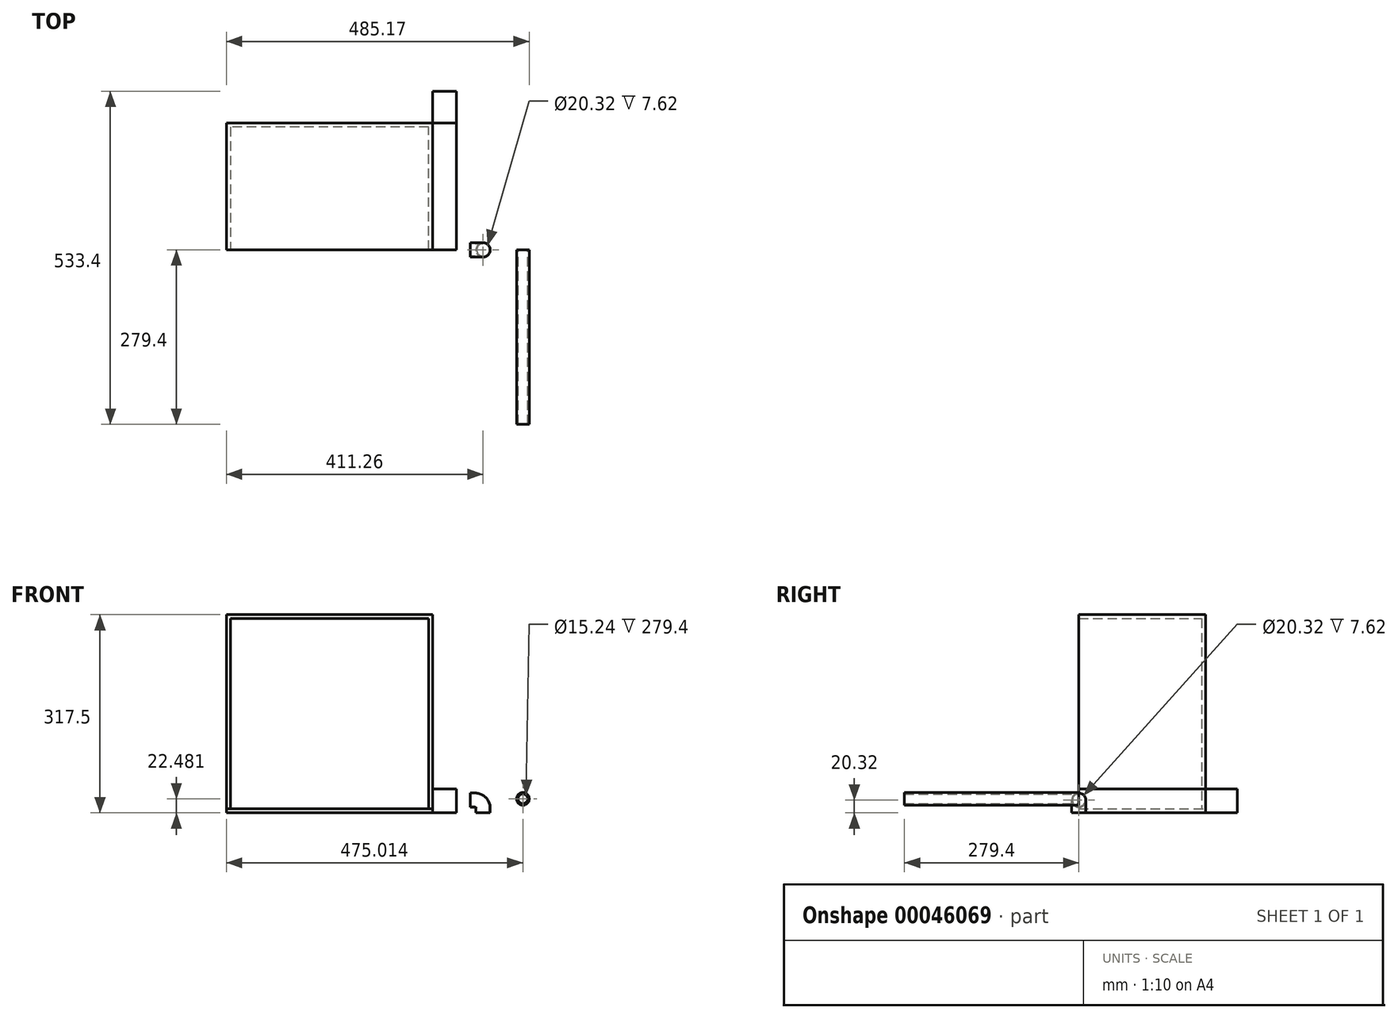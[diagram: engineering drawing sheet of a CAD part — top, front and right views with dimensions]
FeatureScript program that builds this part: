
annotation { "Feature Type Name" : "Feature", "Feature Type Description" : "" }
export const myFeature = defineFeature(function(context is Context, id is Id, definition is map)
    precondition{}
    {
        {
            var Q0;
            Q0=qCreatedBy(makeId("Front.planeOp"),FACE);
            var sketch = newSketch(context, id + "F0", { "sketchPlane" : qUnion([Q0])});
            skLineSegment(sketch, "E0.bottom", {"start": v(0, 0) * mm, "end": v(38.1, 0) * mm});
            skLineSegment(sketch, "E0.top", {"start": v(0, 38.5) * mm, "end": v(38.1, 38.5) * mm});
            skLineSegment(sketch, "E0.left", {"start": v(0, 0) * mm, "end": v(0, 38.5) * mm});
            skLineSegment(sketch, "E0.right", {"start": v(38.1, 0) * mm, "end": v(38.1, 38.5) * mm});
            skSolve(sketch);
        }
        {
            var Q0;
            Q0=makeQuery(id+"F0.imprint","IMPRINT",FACE,{"disambiguationData":[TD([[makeQuery(id+"F0.imprint","IMPRINT",EDGE,{"derivedFrom":sQuery(id+"F0.wireOp",EDGE,"E0.bottom")}),1.0]])]});
            extrude(context, id + "F1", {"entities" : qUnion([Q0]), "oppositeDirection" : true, "depth" : 254 * mm});
        }
        {
            var Q0;
            Q0=makeQuery(id+"F0.imprint","IMPRINT",FACE,{"disambiguationData":[TD([[makeQuery(id+"F0.imprint","IMPRINT",EDGE,{"derivedFrom":sQuery(id+"F0.wireOp",EDGE,"E0.bottom")}),1.0]])]});
            extrude(context, id + "F2", {"entities" : qUnion([Q0]), "oppositeDirection" : true, "depth" : 203.2 * mm});
        }
        {
            var Q0;
            Q0=qCreatedBy(makeId("Top.planeOp"),FACE);
            var sketch = newSketch(context, id + "F3", { "sketchPlane" : qUnion([Q0])});
            skLineSegment(sketch, "E1.bottom", {"start": v(0, 0) * mm, "end": v(-330.2, 0) * mm});
            skLineSegment(sketch, "E1.top", {"start": v(0, 203.2) * mm, "end": v(-330.2, 203.2) * mm});
            skLineSegment(sketch, "E1.left", {"start": v(0, 0) * mm, "end": v(0, 203.2) * mm});
            skLineSegment(sketch, "E1.right", {"start": v(-330.2, 0) * mm, "end": v(-330.2, 203.2) * mm});
            skSolve(sketch);
        }
        {
            var Q0;
            Q0=makeQuery(id+"F3.imprint","IMPRINT",FACE,{"disambiguationData":[TD([[makeQuery(id+"F3.imprint","IMPRINT",EDGE,{"derivedFrom":sQuery(id+"F3.wireOp",EDGE,"E1.bottom")}),-1.0]])]});
            extrude(context, id + "F4", {"entities" : qUnion([Q0]), "depth" : 6.35 * mm});
        }
        {
            var Q0;
            Q0=qCreatedBy(makeId("Front.planeOp"),FACE);
            var sketch = newSketch(context, id + "F5", { "sketchPlane" : qUnion([Q0])});
            skCircle(sketch, "E2", {"center": v(144.81, 22.48) * mm, "radius": 10.16 * mm});
            skCircle(sketch, "E3", {"center": v(144.81, 22.48) * mm, "radius": 7.62 * mm});
            skSolve(sketch);
        }
        {
            var Q0;
            Q0=makeQuery(id+"F5.imprint","IMPRINT",FACE,{"disambiguationData":[TD([[makeQuery(id+"F5.imprint","IMPRINT",EDGE,{"derivedFrom":sQuery(id+"F5.wireOp",EDGE,"E2")}),1.0]])]});
            extrude(context, id + "F6", {"entities" : qUnion([Q0]), "depth" : 279.4 * mm});
        }
        {
            var Q0;
            Q0=qCreatedBy(makeId("Front.planeOp"),FACE);
            var sketch = newSketch(context, id + "F7", { "sketchPlane" : qUnion([Q0])});
            skLineSegment(sketch, "E4", {"start": v(81.06, 0) * mm, "end": v(81.06, 7.62) * mm});
            skArc(sketch, "E5", {"start": v(81.06, 7.62) * mm, "mid": v(77.34, 16.6) * mm, "end": v(68.36, 20.32) * mm});
            skLineSegment(sketch, "E6", {"start": v(68.36, 20.32) * mm, "end": v(60.74, 20.32) * mm});
            skSolve(sketch);
        }
        {
            var Q0;
            Q0=qCreatedBy(makeId("Top.planeOp"),FACE);
            var sketch = newSketch(context, id + "F8", { "sketchPlane" : qUnion([Q0])});
            skCircle(sketch, "E7", {"center": v(81.06, 0) * mm, "radius": 11.43 * mm});
            skCircle(sketch, "E8", {"center": v(81.06, 0) * mm, "radius": 10.16 * mm});
            skSolve(sketch);
        }
        {
            var Q0;
            Q0=makeQuery(id+"F8.imprint","IMPRINT",FACE,{"disambiguationData":[TD([[makeQuery(id+"F8.imprint","IMPRINT",EDGE,{"derivedFrom":sQuery(id+"F8.wireOp",EDGE,"E7")}),1.0]])]});
            var Q1;
            Q1=sQuery(id+"F7.wireOp",EDGE,"E4");
            var Q2;
            Q2=sQuery(id+"F7.wireOp",EDGE,"E5");
            var Q3;
            Q3=sQuery(id+"F7.wireOp",EDGE,"E6");
            sweep(context, id + "F9", {"profiles" : qUnion([Q0]), "path" : qUnion([Q1, Q2, Q3])});
        }
        {
            var Q0;
            Q0=makeQuery(id+"F4.opExtrude","CAP_FACE",FACE,{"disambiguationData":[OSD([sQuery(id+"F3.wireOp",EDGE,"E1.bottom"),sQuery(id+"F3.wireOp",EDGE,"E1.top"),sQuery(id+"F3.wireOp",EDGE,"E1.left"),sQuery(id+"F3.wireOp",EDGE,"E1.right")])],"isStart":false});
            var sketch = newSketch(context, id + "F10", { "sketchPlane" : qUnion([Q0])});
            skLineSegment(sketch, "E9", {"start": v(-330.2, 0) * mm, "end": v(-330.2, 203.2) * mm});
            skLineSegment(sketch, "E10", {"start": v(-330.2, 203.2) * mm, "end": v(0, 203.2) * mm});
            skLineSegment(sketch, "E11", {"start": v(0, 203.2) * mm, "end": v(0, 0) * mm});
            skLineSegment(sketch, "E12", {"start": v(0, 0) * mm, "end": v(-6.35, 0) * mm});
            skLineSegment(sketch, "E13", {"start": v(-6.35, 0) * mm, "end": v(-6.35, 196.85) * mm});
            skLineSegment(sketch, "E14", {"start": v(-6.35, 196.85) * mm, "end": v(-323.85, 196.85) * mm});
            skLineSegment(sketch, "E15", {"start": v(-323.85, 196.85) * mm, "end": v(-323.85, 0) * mm});
            skLineSegment(sketch, "E16", {"start": v(-323.85, 0) * mm, "end": v(-330.2, 0) * mm});
            skLineSegment(sketch, "E17", {"start": v(-323.85, 196.85) * mm, "end": v(-323.85, 203.2) * mm, "construction": true});
            skSolve(sketch);
        }
        {
            var Q0;
            Q0=makeQuery(id+"F10.imprint","IMPRINT",FACE,{"disambiguationData":[TD([[makeQuery(id+"F10.imprint","IMPRINT",EDGE,{"derivedFrom":sQuery(id+"F10.wireOp",EDGE,"E9")}),-1.0]])]});
            extrude(context, id + "F11", {"entities" : qUnion([Q0]), "depth" : 304.8 * mm});
        }
        {
            var Q0;
            Q0=makeQuery(id+"F11.opExtrude","CAP_FACE",FACE,{"disambiguationData":[OSD([sQuery(id+"F10.wireOp",EDGE,"E9"),sQuery(id+"F10.wireOp",EDGE,"E10"),sQuery(id+"F10.wireOp",EDGE,"E11"),sQuery(id+"F10.wireOp",EDGE,"E12"),sQuery(id+"F10.wireOp",EDGE,"E13"),sQuery(id+"F10.wireOp",EDGE,"E14"),sQuery(id+"F10.wireOp",EDGE,"E15"),sQuery(id+"F10.wireOp",EDGE,"E16")])],"isStart":false});
            var sketch = newSketch(context, id + "F12", { "sketchPlane" : qUnion([Q0])});
            skLineSegment(sketch, "E18.bottom", {"start": v(-330.2, 0) * mm, "end": v(0, 0) * mm});
            skLineSegment(sketch, "E18.top", {"start": v(-330.2, 203.2) * mm, "end": v(0, 203.2) * mm});
            skLineSegment(sketch, "E18.left", {"start": v(-330.2, 0) * mm, "end": v(-330.2, 203.2) * mm});
            skLineSegment(sketch, "E18.right", {"start": v(0, 0) * mm, "end": v(0, 203.2) * mm});
            skSolve(sketch);
        }
        {
            var Q0;
            {var subQ1=makeQuery(id+"F11.opExtrude","CAP_EDGE",EDGE,{"disambiguationData":[OSD([sQuery(id+"F10.wireOp",EDGE,"E13")])],"isStart":false});Q0=makeQuery(id+"F12.imprint","IMPRINT",FACE,{"disambiguationData":[TD([[makeQuery(id+"F12.imprint","IMPRINT",EDGE,{"derivedFrom":subQ1}),1.0]])]});}
            var Q1;
            Q1=makeQuery(id+"F12.imprint","IMPRINT",FACE,{"disambiguationData":[TD([[makeQuery(id+"F12.imprint","IMPRINT",EDGE,{"derivedFrom":sQuery(id+"F12.wireOp",EDGE,"E18.top")}),1.0]])]});
            extrude(context, id + "F13", {"entities" : qUnion([Q0, Q1]), "operationType" : NewBodyOperationType.ADD, "depth" : 6.35 * mm});
        }
    });
